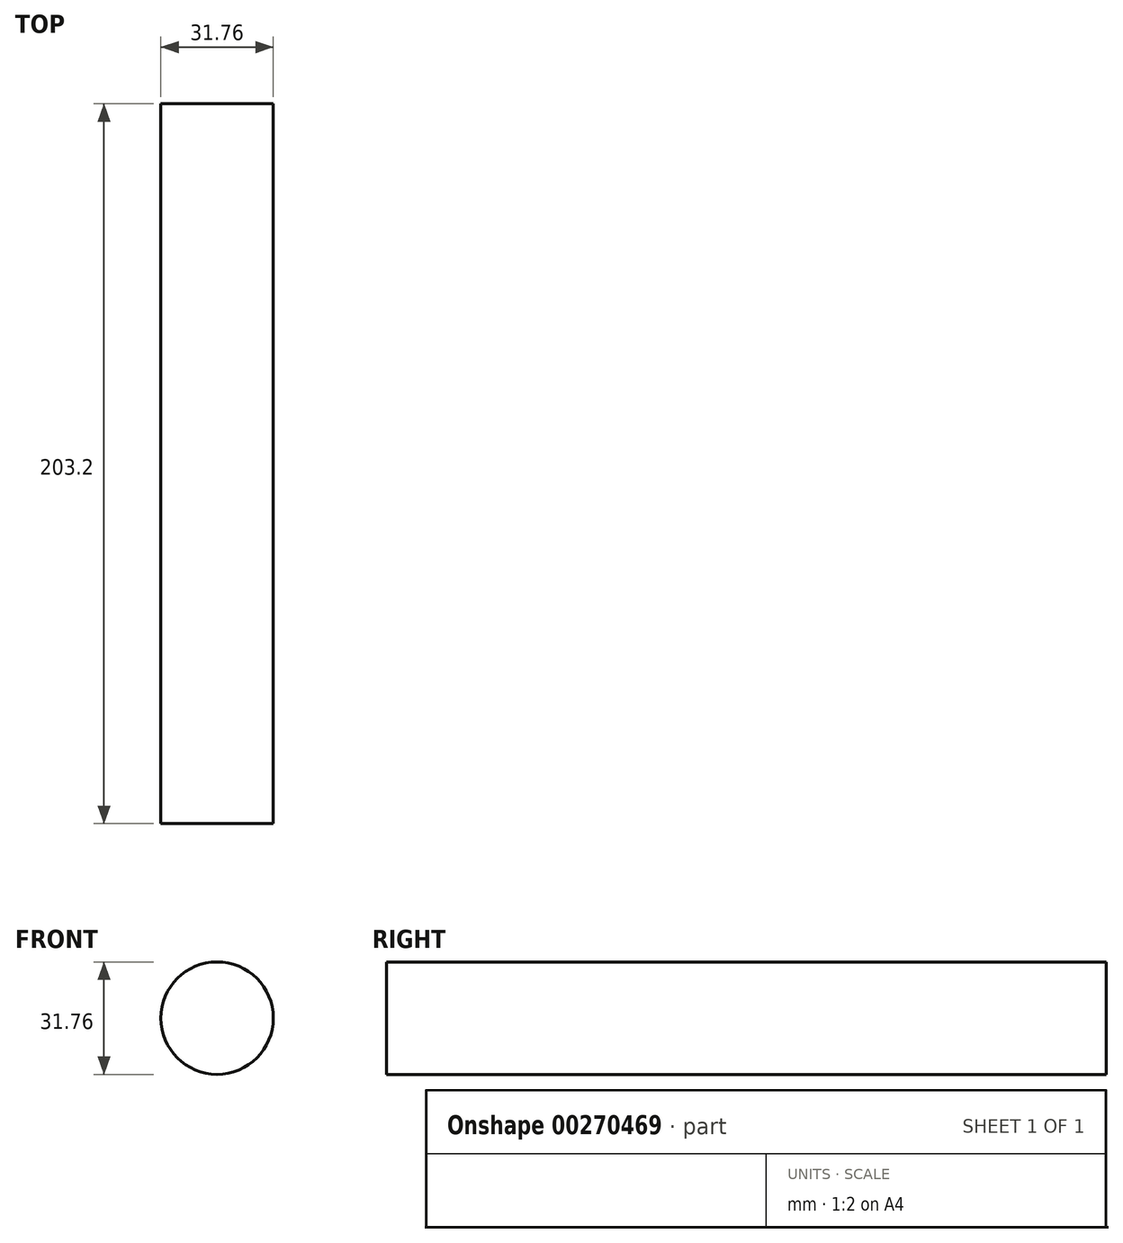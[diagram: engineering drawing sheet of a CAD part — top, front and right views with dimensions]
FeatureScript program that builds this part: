
annotation { "Feature Type Name" : "Feature", "Feature Type Description" : "" }
export const myFeature = defineFeature(function(context is Context, id is Id, definition is map)
    precondition{}
    {
        {
            var Q0;
            Q0=qCreatedBy(makeId("Front.planeOp"),FACE);
            var sketch = newSketch(context, id + "F0", { "sketchPlane" : qUnion([Q0])});
            skCircle(sketch, "E0", {"center": v(0, 0) * mm, "radius": 15.88 * mm});
            skSolve(sketch);
        }
        {
            var Q0;
            Q0 = qSketchRegion(id + "F0", true);
            extrude(context, id + "F1", {"entities" : qUnion([Q0]), "depth" : 203.2 * mm});
        }
    });
